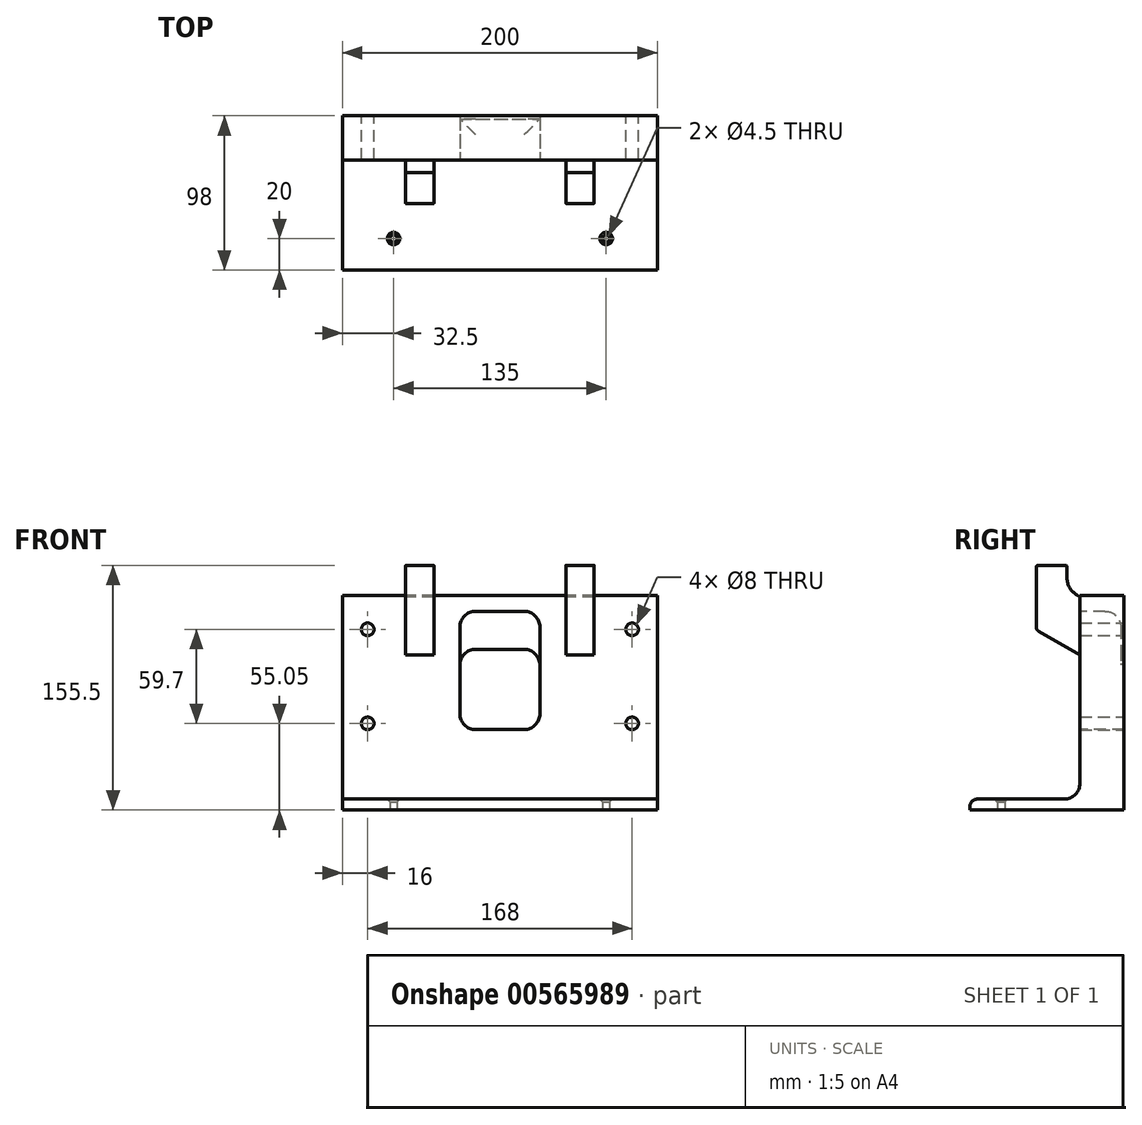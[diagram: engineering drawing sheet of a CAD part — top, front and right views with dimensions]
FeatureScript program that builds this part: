
annotation { "Feature Type Name" : "Feature", "Feature Type Description" : "" }
export const myFeature = defineFeature(function(context is Context, id is Id, definition is map)
    precondition{}
    {
        {
            var Q0;
            Q0=qCreatedBy(makeId("Right.planeOp"),FACE);
            var sketch = newSketch(context, id + "F0", { "sketchPlane" : qUnion([Q0])});
            skLineSegment(sketch, "E0.bottom", {"start": v(-28, 136.25) * mm, "end": v(0, 136.25) * mm});
            skLineSegment(sketch, "E0.top", {"start": v(-28, 0) * mm, "end": v(0, 0) * mm});
            skLineSegment(sketch, "E0.left", {"start": v(-28, 136.25) * mm, "end": v(-28, 17) * mm});
            skLineSegment(sketch, "E0.right", {"start": v(0, 136.25) * mm, "end": v(0, 0) * mm});
            skLineSegment(sketch, "E1.bottom", {"start": v(-28, 0) * mm, "end": v(-98, 0) * mm});
            skLineSegment(sketch, "E1.top", {"start": v(-38, 7) * mm, "end": v(-98, 7) * mm});
            skLineSegment(sketch, "E1.right", {"start": v(-98, 0) * mm, "end": v(-98, 7) * mm});
            skPoint(sketch, "E2.visualSharp", {"position": v(-28, 7) * mm});
            skArc(sketch, "E2.filletArc", {"start": v(-38, 7) * mm, "mid": v(-30.93, 9.93) * mm, "end": v(-28, 17) * mm});
            skSolve(sketch);
        }
        {
            var Q0;
            Q0 = qSketchRegion(id + "F0", true);
            extrude(context, id + "F1", {"entities" : qUnion([Q0]), "endBound" : BoundingType.SYMMETRIC, "depth" : 200 * mm, "offsetDistance" : 25 * mm});
        }
        {
            var Q0;
            Q0=qCreatedBy(makeId("Right.planeOp"),FACE);
            var sketch = newSketch(context, id + "F2", { "sketchPlane" : qUnion([Q0])});
            skLineSegment(sketch, "E3", {"start": v(48.15, 106.49) * mm, "end": v(19.58, 28) * mm});
            skLineSegment(sketch, "E4", {"start": v(19.58, 28) * mm, "end": v(19.58, 0) * mm});
            skLineSegment(sketch, "E5", {"start": v(19.58, 0) * mm, "end": v(0, 0) * mm});
            skLineSegment(sketch, "E6", {"start": v(46.5, 110) * mm, "end": v(0, 126.94) * mm});
            skLineSegment(sketch, "E7", {"start": v(0, 126.94) * mm, "end": v(0, 0) * mm});
            skPoint(sketch, "E8.visualSharp", {"position": v(49.1, 109.07) * mm});
            skArc(sketch, "E8.filletArc", {"start": v(48.15, 106.49) * mm, "mid": v(48.06, 108.59) * mm, "end": v(46.5, 110.01) * mm});
            skLineSegment(sketch, "E9.0", {"start": v(45.25, 107.28) * mm, "end": v(0, 123.74) * mm});
            skLineSegment(sketch, "E9.1", {"start": v(45.25, 107.28) * mm, "end": v(16.58, 28.53) * mm});
            skLineSegment(sketch, "E9.2", {"start": v(16.58, 28.53) * mm, "end": v(16.58, 3) * mm});
            skLineSegment(sketch, "E9.3", {"start": v(16.58, 3) * mm, "end": v(0, 3) * mm});
            skSolve(sketch);
        }
        {
            var Q0;
            Q0=makeQuery(id+"F2.imprint","IMPRINT",FACE,{"disambiguationData":[TD([[makeQuery(id+"F2.imprint","IMPRINT",EDGE,{"derivedFrom":sQuery(id+"F2.wireOp",EDGE,"E3")}),-1.0]])]});
            extrude(context, id + "F3", {"entities" : qUnion([Q0]), "operationType" : NewBodyOperationType.ADD, "endBound" : BoundingType.SYMMETRIC, "depth" : 85 * mm, "offsetDistance" : 25 * mm});
        }
        {
            var Q0;
            Q0=makeQuery(id+"F3.opExtrude","SWEPT_FACE",FACE,{"disambiguationData":[OSD([sQuery(id+"F2.wireOp",EDGE,"E3")])]});
            var sketch = newSketch(context, id + "F4", { "sketchPlane" : qUnion([Q0])});
            skLineSegment(sketch, "E10.bottom", {"start": v(-9.95, 93.91) * mm, "end": v(9.95, 93.91) * mm});
            skLineSegment(sketch, "E10.top", {"start": v(-9.95, 62.51) * mm, "end": v(9.95, 62.51) * mm});
            skLineSegment(sketch, "E10.left", {"start": v(-15.7, 88.16) * mm, "end": v(-15.7, 68.26) * mm});
            skLineSegment(sketch, "E10.right", {"start": v(15.7, 88.16) * mm, "end": v(15.7, 68.26) * mm});
            skLineSegment(sketch, "E11", {"start": v(0, 62.51) * mm, "end": v(0, 0) * mm, "construction": true});
            skCircle(sketch, "E12", {"center": v(19.05, 108.21) * mm, "radius": 2.1 * mm});
            skCircle(sketch, "E13", {"center": v(9.53, 108.21) * mm, "radius": 2.4 * mm});
            skCircle(sketch, "E14", {"center": v(-19.05, 108.21) * mm, "radius": 2.1 * mm});
            skCircle(sketch, "E15", {"center": v(-19.05, 48.21) * mm, "radius": 2.1 * mm});
            skCircle(sketch, "E16", {"center": v(9.53, 48.21) * mm, "radius": 2.4 * mm});
            skCircle(sketch, "E17", {"center": v(19.05, 48.21) * mm, "radius": 2.1 * mm});
            skPoint(sketch, "E18.visualSharp", {"position": v(-15.7, 93.91) * mm});
            skArc(sketch, "E18.filletArc", {"start": v(-9.95, 93.91) * mm, "mid": v(-14.02, 92.23) * mm, "end": v(-15.7, 88.16) * mm});
            skPoint(sketch, "E19.visualSharp", {"position": v(15.7, 93.91) * mm});
            skArc(sketch, "E19.filletArc", {"start": v(15.7, 88.16) * mm, "mid": v(14.02, 92.23) * mm, "end": v(9.95, 93.91) * mm});
            skPoint(sketch, "E20.visualSharp", {"position": v(-15.7, 62.51) * mm});
            skArc(sketch, "E20.filletArc", {"start": v(-15.7, 68.26) * mm, "mid": v(-14.02, 64.2) * mm, "end": v(-9.95, 62.51) * mm});
            skPoint(sketch, "E21.visualSharp", {"position": v(15.7, 62.51) * mm});
            skArc(sketch, "E21.filletArc", {"start": v(9.95, 62.51) * mm, "mid": v(14.02, 64.2) * mm, "end": v(15.7, 68.26) * mm});
            skCircle(sketch, "E22", {"center": v(-33, 78.21) * mm, "radius": 2.75 * mm});
            skPoint(sketch, "E22.centerSnap0", {"position": v(-15.7, 78.21) * mm});
            skCircle(sketch, "E23", {"center": v(33, 78.21) * mm, "radius": 2.75 * mm});
            skPoint(sketch, "E23.centerSnap0", {"position": v(15.7, 78.21) * mm});
            skLineSegment(sketch, "E24", {"start": v(0, 78.21) * mm, "end": v(-33, 78.21) * mm, "construction": true});
            skLineSegment(sketch, "E25", {"start": v(0, 78.21) * mm, "end": v(33, 78.21) * mm, "construction": true});
            skSolve(sketch);
        }
        {
            var Q0;
            Q0 = qSketchRegion(id + "F4", true);
            extrude(context, id + "F5", {"entities" : qUnion([Q0]), "operationType" : NewBodyOperationType.REMOVE, "oppositeDirection" : true, "depth" : 25 * mm, "offsetDistance" : 25 * mm});
        }
        {
            var Q0;
            Q0=makeQuery(id+"F3.opExtrude","CAP_FACE",FACE,{"disambiguationData":[OSD([sQuery(id+"F2.wireOp",EDGE,"E3"),sQuery(id+"F2.wireOp",EDGE,"E4"),sQuery(id+"F2.wireOp",EDGE,"E5"),sQuery(id+"F2.wireOp",EDGE,"E6"),sQuery(id+"F2.wireOp",EDGE,"E7"),sQuery(id+"F2.wireOp",EDGE,"E8.filletArc"),sQuery(id+"F2.wireOp",EDGE,"E9.0"),sQuery(id+"F2.wireOp",EDGE,"E9.1"),sQuery(id+"F2.wireOp",EDGE,"E9.2"),sQuery(id+"F2.wireOp",EDGE,"E9.3")])],"isStart":false});
            var sketch = newSketch(context, id + "F6", { "sketchPlane" : qUnion([Q0])});
            skLineSegment(sketch, "E26", {"start": v(0, 126.94) * mm, "end": v(46.5, 110) * mm});
            skLineSegment(sketch, "E27", {"start": v(48.15, 106.49) * mm, "end": v(19.58, 28) * mm});
            skLineSegment(sketch, "E28", {"start": v(19.58, 28) * mm, "end": v(19.58, 0) * mm});
            skLineSegment(sketch, "E29", {"start": v(19.58, 0) * mm, "end": v(0, 0) * mm});
            skLineSegment(sketch, "E30", {"start": v(0, 0) * mm, "end": v(0, 126.94) * mm});
            skArc(sketch, "E31", {"start": v(48.15, 106.49) * mm, "mid": v(48.06, 108.59) * mm, "end": v(46.5, 110) * mm});
            skSolve(sketch);
        }
        {
            var Q0;
            Q0 = qSketchRegion(id + "F6", true);
            extrude(context, id + "F7", {"entities" : qUnion([Q0]), "operationType" : NewBodyOperationType.ADD, "depth" : 5 * mm, "offsetDistance" : 25 * mm});
        }
        {
            var Q0;
            Q0=makeQuery(id+"F3.opExtrude","CAP_FACE",FACE,{"disambiguationData":[OSD([sQuery(id+"F2.wireOp",EDGE,"E3"),sQuery(id+"F2.wireOp",EDGE,"E4"),sQuery(id+"F2.wireOp",EDGE,"E5"),sQuery(id+"F2.wireOp",EDGE,"E6"),sQuery(id+"F2.wireOp",EDGE,"E7"),sQuery(id+"F2.wireOp",EDGE,"E8.filletArc"),sQuery(id+"F2.wireOp",EDGE,"E9.0"),sQuery(id+"F2.wireOp",EDGE,"E9.1"),sQuery(id+"F2.wireOp",EDGE,"E9.2"),sQuery(id+"F2.wireOp",EDGE,"E9.3")])],"isStart":true});
            var sketch = newSketch(context, id + "F8", { "sketchPlane" : qUnion([Q0])});
            skLineSegment(sketch, "E32", {"start": v(-46.5, 110) * mm, "end": v(0, 126.94) * mm});
            skLineSegment(sketch, "E33", {"start": v(0, 126.94) * mm, "end": v(0, 0) * mm});
            skLineSegment(sketch, "E34", {"start": v(0, 0) * mm, "end": v(-19.58, 0) * mm});
            skLineSegment(sketch, "E35", {"start": v(-19.58, 0) * mm, "end": v(-19.58, 28) * mm});
            skLineSegment(sketch, "E36", {"start": v(-19.58, 28) * mm, "end": v(-48.15, 106.49) * mm});
            skArc(sketch, "E37", {"start": v(-46.5, 110) * mm, "mid": v(-48.06, 108.59) * mm, "end": v(-48.15, 106.49) * mm});
            skSolve(sketch);
        }
        {
            var Q0;
            Q0 = qSketchRegion(id + "F8", true);
            extrude(context, id + "F9", {"entities" : qUnion([Q0]), "operationType" : NewBodyOperationType.ADD, "depth" : 5 * mm, "offsetDistance" : 25 * mm});
        }
        {
            var Q0;
            Q0=makeQuery(id+"F1.opExtrude","SWEPT_FACE",FACE,{"disambiguationData":[OSD([sQuery(id+"F0.wireOp",EDGE,"E0.left")])]});
            var sketch = newSketch(context, id + "F10", { "sketchPlane" : qUnion([Q0])});
            skLineSegment(sketch, "E38.bottom", {"start": v(-15.38, 126.25) * mm, "end": v(15.38, 126.25) * mm});
            skLineSegment(sketch, "E38.top", {"start": v(-15.38, 51.1) * mm, "end": v(15.38, 51.1) * mm});
            skLineSegment(sketch, "E38.left", {"start": v(-25.38, 116.25) * mm, "end": v(-25.38, 61.1) * mm});
            skLineSegment(sketch, "E38.right", {"start": v(25.38, 116.25) * mm, "end": v(25.38, 61.1) * mm});
            skPoint(sketch, "E39.visualSharp", {"position": v(-25.38, 126.25) * mm});
            skArc(sketch, "E39.filletArc", {"start": v(-15.38, 126.25) * mm, "mid": v(-22.45, 123.32) * mm, "end": v(-25.38, 116.25) * mm});
            skPoint(sketch, "E40.visualSharp", {"position": v(25.38, 126.25) * mm});
            skArc(sketch, "E40.filletArc", {"start": v(25.38, 116.25) * mm, "mid": v(22.45, 123.32) * mm, "end": v(15.38, 126.25) * mm});
            skPoint(sketch, "E41.visualSharp", {"position": v(25.38, 51.1) * mm});
            skArc(sketch, "E41.filletArc", {"start": v(15.38, 51.1) * mm, "mid": v(22.45, 54.03) * mm, "end": v(25.38, 61.1) * mm});
            skPoint(sketch, "E42.visualSharp", {"position": v(-25.38, 51.1) * mm});
            skArc(sketch, "E42.filletArc", {"start": v(-25.38, 61.1) * mm, "mid": v(-22.45, 54.03) * mm, "end": v(-15.37, 51.1) * mm});
            skLineSegment(sketch, "E43", {"start": v(0, 0) * mm, "end": v(0, 51.1) * mm, "construction": true});
            skPoint(sketch, "E43.endSnap0", {"position": v(0, 51.1) * mm});
            skSolve(sketch);
        }
        {
            var Q0;
            Q0 = qSketchRegion(id + "F10", true);
            extrude(context, id + "F11", {"entities" : qUnion([Q0]), "operationType" : NewBodyOperationType.REMOVE, "oppositeDirection" : true, "depth" : 26 * mm, "offsetDistance" : 25 * mm});
        }
        {
            var Q0;
            Q0=makeQuery(id+"F11.boolean.opBoolean","COPY",FACE,{"derivedFrom":makeQuery(id+"F11.opExtrude","CAP_FACE",FACE,{"disambiguationData":[OSD([sQuery(id+"F10.wireOp",EDGE,"E38.bottom"),sQuery(id+"F10.wireOp",EDGE,"E38.top"),sQuery(id+"F10.wireOp",EDGE,"E38.left"),sQuery(id+"F10.wireOp",EDGE,"E38.right"),sQuery(id+"F10.wireOp",EDGE,"E39.filletArc"),sQuery(id+"F10.wireOp",EDGE,"E40.filletArc"),sQuery(id+"F10.wireOp",EDGE,"E41.filletArc"),sQuery(id+"F10.wireOp",EDGE,"E42.filletArc")])],"isStart":false})});
            var sketch = newSketch(context, id + "F12", { "sketchPlane" : qUnion([Q0])});
            skLineSegment(sketch, "E44.bottom", {"start": v(-15.38, 102.1) * mm, "end": v(15.38, 102.1) * mm});
            skLineSegment(sketch, "E44.top", {"start": v(-15.38, 51.1) * mm, "end": v(15.38, 51.1) * mm});
            skLineSegment(sketch, "E44.left", {"start": v(-25.38, 92.1) * mm, "end": v(-25.38, 61.1) * mm});
            skLineSegment(sketch, "E44.right", {"start": v(25.38, 92.1) * mm, "end": v(25.38, 61.1) * mm});
            skPoint(sketch, "E45.visualSharp", {"position": v(-25.38, 102.1) * mm});
            skArc(sketch, "E45.filletArc", {"start": v(-15.38, 102.1) * mm, "mid": v(-22.45, 99.17) * mm, "end": v(-25.38, 92.1) * mm});
            skPoint(sketch, "E46.visualSharp", {"position": v(25.38, 102.1) * mm});
            skArc(sketch, "E46.filletArc", {"start": v(25.38, 92.1) * mm, "mid": v(22.45, 99.17) * mm, "end": v(15.38, 102.1) * mm});
            skPoint(sketch, "E47.visualSharp", {"position": v(25.38, 51.1) * mm});
            skArc(sketch, "E47.filletArc", {"start": v(15.38, 51.1) * mm, "mid": v(22.45, 54.03) * mm, "end": v(25.38, 61.1) * mm});
            skPoint(sketch, "E48.visualSharp", {"position": v(-25.38, 51.1) * mm});
            skArc(sketch, "E48.filletArc", {"start": v(-25.38, 61.1) * mm, "mid": v(-22.45, 54.03) * mm, "end": v(-15.38, 51.1) * mm});
            skSolve(sketch);
        }
        {
            var Q0;
            Q0 = qSketchRegion(id + "F12", true);
            extrude(context, id + "F13", {"entities" : qUnion([Q0]), "operationType" : NewBodyOperationType.REMOVE, "oppositeDirection" : true, "depth" : 3 * mm, "offsetDistance" : 25 * mm});
        }
        {
            var Q0;
            Q0=makeQuery(id+"F9.boolean.opBoolean","MERGE",EDGE,{"derivedFrom":[makeQuery(id+"F7.boolean.opBoolean","MERGE",EDGE,{"derivedFrom":[makeQuery(id+"F3.opExtrude","SWEPT_EDGE",EDGE,{"disambiguationData":[OSD([sQuery(id+"F2.wireOp",EDGE,"E6"),sQuery(id+"F2.wireOp",EDGE,"E7")])]}),makeQuery(id+"F7.opExtrude","SWEPT_EDGE",EDGE,{"disambiguationData":[OSD([sQuery(id+"F6.wireOp",EDGE,"E26"),sQuery(id+"F6.wireOp",EDGE,"E30")])]})]}),makeQuery(id+"F9.opExtrude","SWEPT_EDGE",EDGE,{"disambiguationData":[OSD([sQuery(id+"F8.wireOp",EDGE,"E32"),sQuery(id+"F8.wireOp",EDGE,"E33")])]})]});
            var Q1;
            Q1=makeQuery(id+"F9.boolean.opBoolean","MERGE",EDGE,{"derivedFrom":[makeQuery(id+"F7.boolean.opBoolean","MERGE",EDGE,{"derivedFrom":[makeQuery(id+"F3.opExtrude","SWEPT_EDGE",EDGE,{"disambiguationData":[OSD([sQuery(id+"F2.wireOp",EDGE,"E3"),sQuery(id+"F2.wireOp",EDGE,"E4")])]}),makeQuery(id+"F7.opExtrude","SWEPT_EDGE",EDGE,{"disambiguationData":[OSD([sQuery(id+"F6.wireOp",EDGE,"E27"),sQuery(id+"F6.wireOp",EDGE,"E28")])]})]}),makeQuery(id+"F9.opExtrude","SWEPT_EDGE",EDGE,{"disambiguationData":[OSD([sQuery(id+"F8.wireOp",EDGE,"E35"),sQuery(id+"F8.wireOp",EDGE,"E36")])]})]});
            fillet(context, id + "F14", {"entities" : qUnion([Q0, Q1]), "tangentPropagation" : true, "radius" : 11.32 * mm, "defaultsChanged" : false, "vertexSettings" : [], "allowEdgeOverflow" : false});
        }
        {
            var Q0;
            Q0=qCreatedBy(makeId("Right.planeOp"),FACE);
            var sketch = newSketch(context, id + "F15", { "sketchPlane" : qUnion([Q0])});
            skLineSegment(sketch, "E49", {"start": v(-28, 98.4) * mm, "end": v(-54.2, 113.52) * mm});
            skLineSegment(sketch, "E50", {"start": v(-55.7, 116.12) * mm, "end": v(-55.7, 154.5) * mm});
            skLineSegment(sketch, "E51", {"start": v(-54.7, 155.5) * mm, "end": v(-37.2, 155.5) * mm});
            skLineSegment(sketch, "E52", {"start": v(-36.2, 154.5) * mm, "end": v(-36.2, 147.42) * mm});
            skLineSegment(sketch, "E53", {"start": v(-29.95, 136.6) * mm, "end": v(-28, 135.47) * mm});
            skLineSegment(sketch, "E54", {"start": v(-28, 135.47) * mm, "end": v(-28, 98.4) * mm});
            skPoint(sketch, "E55.visualSharp", {"position": v(-55.7, 114.39) * mm});
            skArc(sketch, "E55.filletArc", {"start": v(-55.7, 116.12) * mm, "mid": v(-55.3, 114.62) * mm, "end": v(-54.2, 113.52) * mm});
            skPoint(sketch, "E56.visualSharp", {"position": v(-55.7, 155.5) * mm});
            skArc(sketch, "E56.filletArc", {"start": v(-54.7, 155.5) * mm, "mid": v(-55.4, 155.2) * mm, "end": v(-55.7, 154.5) * mm});
            skPoint(sketch, "E57.visualSharp", {"position": v(-36.2, 155.5) * mm});
            skArc(sketch, "E57.filletArc", {"start": v(-36.2, 154.5) * mm, "mid": v(-36.5, 155.2) * mm, "end": v(-37.2, 155.5) * mm});
            skPoint(sketch, "E58.visualSharp", {"position": v(-36.2, 140.2) * mm});
            skArc(sketch, "E58.filletArc", {"start": v(-36.2, 147.42) * mm, "mid": v(-34.53, 141.17) * mm, "end": v(-29.95, 136.6) * mm});
            skSolve(sketch);
        }
        {
            var Q0;
            Q0 = qSketchRegion(id + "F15", true);
            extrude(context, id + "F16", {"entities" : qUnion([Q0]), "operationType" : NewBodyOperationType.ADD, "endBound" : BoundingType.SYMMETRIC, "depth" : 119.75 * mm, "offsetDistance" : 25 * mm});
        }
        {
            var Q0;
            Q0 = qSketchRegion(id + "F15", true);
            extrude(context, id + "F17", {"entities" : qUnion([Q0]), "operationType" : NewBodyOperationType.REMOVE, "endBound" : BoundingType.SYMMETRIC, "oppositeDirection" : true, "depth" : 83.75 * mm, "offsetDistance" : 25 * mm});
        }
        {
            var Q0;
            {var subQ3=sQuery(id+"F0.wireOp",EDGE,"E0.bottom");var subQ8=sQuery(id+"F0.wireOp",EDGE,"E0.right");Q0=makeQuery(id+"F9.boolean.opBoolean","SPLIT",FACE,{"disambiguationData":[TD([makeQuery(id+"F1.opExtrude","SWEPT_FACE",FACE,{"disambiguationData":[OSD([subQ3])]})])],"derivedFrom":makeQuery(id+"F1.opExtrude","SWEPT_FACE",FACE,{"disambiguationData":[OSD([subQ8])]})});}
            var sketch = newSketch(context, id + "F18", { "sketchPlane" : qUnion([Q0])});
            skLineSegment(sketch, "E59.bottom", {"start": v(-42.5, 106.49) * mm, "end": v(42.5, 106.49) * mm});
            skLineSegment(sketch, "E59.top", {"start": v(-42.5, 136.25) * mm, "end": v(42.5, 136.25) * mm});
            skLineSegment(sketch, "E59.left", {"start": v(-42.5, 106.49) * mm, "end": v(-42.5, 136.25) * mm});
            skLineSegment(sketch, "E59.right", {"start": v(42.5, 106.49) * mm, "end": v(42.5, 136.25) * mm});
            skSolve(sketch);
        }
        {
            var Q0;
            Q0 = qSketchRegion(id + "F18", true);
            extrude(context, id + "F19", {"entities" : qUnion([Q0]), "operationType" : NewBodyOperationType.REMOVE, "depth" : 100.8 * mm, "offsetDistance" : 25 * mm});
        }
        {
            var Q0;
            Q0=makeQuery(id+"F19.boolean.opBoolean","MERGE",EDGE,{"derivedFrom":[makeQuery(id+"F9.opExtrude","CAP_EDGE",EDGE,{"disambiguationData":[OSD([sQuery(id+"F8.wireOp",EDGE,"E33")])],"isStart":true})],"fromTools":[makeQuery(id+"F19.opExtrude","CAP_EDGE",EDGE,{"disambiguationData":[OSD([sQuery(id+"F18.wireOp",EDGE,"E59.right")])],"isStart":true})]});
            var Q1;
            Q1=makeQuery(id+"F3.opExtrude","CAP_EDGE",EDGE,{"disambiguationData":[OSD([sQuery(id+"F2.wireOp",EDGE,"E9.1")])],"isStart":true});
            var Q2;
            Q2=makeQuery(id+"F3.opExtrude","CAP_EDGE",EDGE,{"disambiguationData":[OSD([sQuery(id+"F2.wireOp",EDGE,"E9.2")])],"isStart":true});
            var Q3;
            Q3=makeQuery(id+"F19.boolean.opBoolean","MERGE",EDGE,{"derivedFrom":[makeQuery(id+"F7.opExtrude","CAP_EDGE",EDGE,{"disambiguationData":[OSD([sQuery(id+"F6.wireOp",EDGE,"E30")])],"isStart":true})],"fromTools":[makeQuery(id+"F19.opExtrude","CAP_EDGE",EDGE,{"disambiguationData":[OSD([sQuery(id+"F18.wireOp",EDGE,"E59.left")])],"isStart":true})]});
            var Q4;
            Q4=makeQuery(id+"F3.opExtrude","CAP_EDGE",EDGE,{"disambiguationData":[OSD([sQuery(id+"F2.wireOp",EDGE,"E9.1")])],"isStart":false});
            var Q5;
            Q5=makeQuery(id+"F3.opExtrude","CAP_EDGE",EDGE,{"disambiguationData":[OSD([sQuery(id+"F2.wireOp",EDGE,"E9.2")])],"isStart":false});
            var Q6;
            Q6=makeQuery(id+"F7.opExtrude","CAP_EDGE",EDGE,{"disambiguationData":[OSD([sQuery(id+"F6.wireOp",EDGE,"E30")])],"isStart":false});
            var Q7;
            Q7=makeQuery(id+"F9.opExtrude","CAP_EDGE",EDGE,{"disambiguationData":[OSD([sQuery(id+"F8.wireOp",EDGE,"E33")])],"isStart":false});
            fillet(context, id + "F20", {"entities" : qUnion([Q0, Q1, Q2, Q3, Q4, Q5, Q6, Q7]), "tangentPropagation" : true, "radius" : 5 * mm, "defaultsChanged" : false, "vertexSettings" : [], "allowEdgeOverflow" : false});
        }
        {
            var Q0;
            Q0=makeQuery(id+"F3.opExtrude","SWEPT_EDGE",EDGE,{"disambiguationData":[OSD([sQuery(id+"F2.wireOp",EDGE,"E7"),sQuery(id+"F2.wireOp",EDGE,"E9.3")])]});
            var Q1;
            Q1=makeQuery(id+"F19.boolean.opBoolean","COPY",EDGE,{"derivedFrom":makeQuery(id+"F19.opExtrude","SWEPT_EDGE",EDGE,{"disambiguationData":[OSD([sQuery(id+"F18.wireOp",EDGE,"E59.bottom"),sQuery(id+"F18.wireOp",EDGE,"E59.left")])]})});
            var Q2;
            Q2=makeQuery(id+"F19.boolean.opBoolean","COPY",EDGE,{"derivedFrom":makeQuery(id+"F19.opExtrude","SWEPT_EDGE",EDGE,{"disambiguationData":[OSD([sQuery(id+"F18.wireOp",EDGE,"E59.bottom"),sQuery(id+"F18.wireOp",EDGE,"E59.right")])]})});
            var Q3;
            {var subQ0=sQuery(id+"F15.wireOp",EDGE,"E54");var subQ1=sQuery(id+"F15.wireOp",EDGE,"E49");var subQ2=makeQuery(id+"F16.opExtrude","SWEPT_FACE",FACE,{"disambiguationData":[OSD([subQ1])]});var subQ3=makeQuery(id+"F1.opExtrude","SWEPT_FACE",FACE,{"disambiguationData":[OSD([sQuery(id+"F0.wireOp",EDGE,"E0.left")])]});Q3=makeQuery(id+"F16.boolean.opBoolean","SPLIT",EDGE,{"disambiguationData":[topologyDisambiguationEdgeConnected([subQ3,subQ2]),TD([makeQuery(id+"F11.boolean.opBoolean","COPY",FACE,{"derivedFrom":makeQuery(id+"F11.opExtrude","SWEPT_FACE",FACE,{"disambiguationData":[OSD([sQuery(id+"F10.wireOp",EDGE,"E38.left")])]})})])],"derivedFrom":makeQuery(id+"F16.opExtrude","SWEPT_EDGE",EDGE,{"disambiguationData":[OSD([subQ1,subQ0])]})});}
            var Q4;
            {var subQ0=sQuery(id+"F15.wireOp",EDGE,"E54");var subQ1=sQuery(id+"F15.wireOp",EDGE,"E49");var subQ2=makeQuery(id+"F16.opExtrude","SWEPT_FACE",FACE,{"disambiguationData":[OSD([subQ1])]});var subQ3=makeQuery(id+"F1.opExtrude","SWEPT_FACE",FACE,{"disambiguationData":[OSD([sQuery(id+"F0.wireOp",EDGE,"E0.left")])]});Q4=makeQuery(id+"F16.boolean.opBoolean","SPLIT",EDGE,{"disambiguationData":[topologyDisambiguationEdgeConnected([subQ3,subQ2]),TD([makeQuery(id+"F11.boolean.opBoolean","COPY",FACE,{"derivedFrom":makeQuery(id+"F11.opExtrude","SWEPT_FACE",FACE,{"disambiguationData":[OSD([sQuery(id+"F10.wireOp",EDGE,"E38.right")])]})})])],"derivedFrom":makeQuery(id+"F16.opExtrude","SWEPT_EDGE",EDGE,{"disambiguationData":[OSD([subQ1,subQ0])]})});}
            var Q5;
            Q5=makeQuery(id+"F16.opExtrude","CAP_EDGE",EDGE,{"disambiguationData":[OSD([sQuery(id+"F15.wireOp",EDGE,"E54")])],"isStart":false});
            var Q6;
            Q6=makeQuery(id+"F16.opExtrude","CAP_EDGE",EDGE,{"disambiguationData":[OSD([sQuery(id+"F15.wireOp",EDGE,"E54")])],"isStart":true});
            var Q7;
            Q7=makeQuery(id+"F1.opExtrude","SWEPT_EDGE",EDGE,{"disambiguationData":[OSD([sQuery(id+"F0.wireOp",EDGE,"E1.top"),sQuery(id+"F0.wireOp",EDGE,"E1.right")])]});
            fillet(context, id + "F21", {"entities" : qUnion([Q0, Q1, Q2, Q3, Q4, Q5, Q6, Q7]), "tangentPropagation" : true, "radius" : 5 * mm, "defaultsChanged" : false, "vertexSettings" : [], "allowEdgeOverflow" : false});
        }
        {
            var Q0;
            Q0=makeQuery(id+"F11.boolean.opBoolean","COPY",EDGE,{"derivedFrom":makeQuery(id+"F11.opExtrude","CAP_EDGE",EDGE,{"disambiguationData":[OSD([sQuery(id+"F10.wireOp",EDGE,"E38.bottom")])],"isStart":false})});
            fillet(context, id + "F22", {"entities" : qUnion([Q0]), "radius" : 10 * mm, "defaultsChanged" : true, "vertexSettings" : [], "allowEdgeOverflow" : false});
        }
        {
            var Q0;
            Q0=qCreatedBy(makeId("Top.planeOp"),FACE);
            var sketch = newSketch(context, id + "F23", { "sketchPlane" : qUnion([Q0])});
            skCircle(sketch, "E60", {"center": v(-67.5, -78) * mm, "radius": 2.25 * mm});
            skCircle(sketch, "E61", {"center": v(67.5, -78) * mm, "radius": 2.25 * mm});
            skLineSegment(sketch, "E62", {"start": v(0, 0) * mm, "end": v(-67.5, -78) * mm, "construction": true});
            skLineSegment(sketch, "E63", {"start": v(0, 0) * mm, "end": v(67.5, -78) * mm, "construction": true});
            skLineSegment(sketch, "E64", {"start": v(-67.5, -78) * mm, "end": v(67.5, -78) * mm, "construction": true});
            skLineSegment(sketch, "E65", {"start": v(0, -78) * mm, "end": v(0, 0) * mm, "construction": true});
            skSolve(sketch);
        }
        {
            var Q0;
            Q0 = qSketchRegion(id + "F23", true);
            extrude(context, id + "F24", {"entities" : qUnion([Q0]), "operationType" : NewBodyOperationType.REMOVE, "depth" : 25 * mm, "offsetDistance" : 25 * mm});
        }
        {
            var Q0;
            Q0=makeQuery(id+"F24.boolean.opBoolean","INTERSECT",EDGE,{"derivedFrom":[makeQuery(id+"F1.opExtrude","SWEPT_FACE",FACE,{"disambiguationData":[OSD([sQuery(id+"F0.wireOp",EDGE,"E1.top")])]}),makeQuery(id+"F24.opExtrude","SWEPT_FACE",FACE,{"disambiguationData":[OSD([sQuery(id+"F23.wireOp",EDGE,"E60")])]})]});
            var Q1;
            Q1=makeQuery(id+"F24.boolean.opBoolean","INTERSECT",EDGE,{"derivedFrom":[makeQuery(id+"F1.opExtrude","SWEPT_FACE",FACE,{"disambiguationData":[OSD([sQuery(id+"F0.wireOp",EDGE,"E1.top")])]}),makeQuery(id+"F24.opExtrude","SWEPT_FACE",FACE,{"disambiguationData":[OSD([sQuery(id+"F23.wireOp",EDGE,"E61")])]})]});
            chamfer(context, id + "F25", {"entities" : qUnion([Q0, Q1]), "width" : 1.7 * mm, "tangentPropagation" : true});
        }
        {
            var Q0;
            Q0=qCreatedBy(makeId("Right.planeOp"),FACE);
            var sketch = newSketch(context, id + "F26", { "sketchPlane" : qUnion([Q0])});
            skLineSegment(sketch, "E66.bottom", {"start": v(48.32, 136.25) * mm, "end": v(0, 136.25) * mm});
            skLineSegment(sketch, "E66.top", {"start": v(48.32, 0) * mm, "end": v(0, 0) * mm});
            skLineSegment(sketch, "E66.left", {"start": v(48.32, 136.25) * mm, "end": v(48.32, 0) * mm});
            skLineSegment(sketch, "E66.right", {"start": v(0, 136.25) * mm, "end": v(0, 0) * mm});
            skSolve(sketch);
        }
        {
            var Q0;
            Q0 = qSketchRegion(id + "F26", true);
            extrude(context, id + "F27", {"entities" : qUnion([Q0]), "operationType" : NewBodyOperationType.REMOVE, "endBound" : BoundingType.SYMMETRIC, "oppositeDirection" : true, "depth" : 200 * mm, "offsetDistance" : 25 * mm});
        }
        {
            var Q0;
            {var subQ7=sQuery(id+"F0.wireOp",EDGE,"E0.bottom");var subQ12=sQuery(id+"F0.wireOp",EDGE,"E0.right");var subQ20=makeQuery(id+"F1.opExtrude","SWEPT_FACE",FACE,{"disambiguationData":[OSD([subQ12])]});Q0=makeQuery(id+"F27.boolean.opBoolean","MERGE",FACE,{"derivedFrom":[makeQuery(id+"F19.boolean.opBoolean","MERGE",FACE,{"derivedFrom":[makeQuery(id+"F9.boolean.opBoolean","SPLIT",FACE,{"disambiguationData":[TD([makeQuery(id+"F3.opExtrude","SWEPT_FACE",FACE,{"disambiguationData":[OSD([sQuery(id+"F2.wireOp",EDGE,"E9.0")])]})])],"derivedFrom":subQ20}),makeQuery(id+"F9.boolean.opBoolean","SPLIT",FACE,{"disambiguationData":[TD([makeQuery(id+"F1.opExtrude","SWEPT_FACE",FACE,{"disambiguationData":[OSD([subQ7])]})])],"derivedFrom":subQ20})],"fromTools":[makeQuery(id+"F19.opExtrude","CAP_FACE",FACE,{"disambiguationData":[OSD([sQuery(id+"F18.wireOp",EDGE,"E59.bottom"),sQuery(id+"F18.wireOp",EDGE,"E59.top"),sQuery(id+"F18.wireOp",EDGE,"E59.left"),sQuery(id+"F18.wireOp",EDGE,"E59.right")])],"isStart":true})]})],"fromTools":[makeQuery(id+"F27.opExtrude","SWEPT_FACE",FACE,{"disambiguationData":[OSD([sQuery(id+"F26.wireOp",EDGE,"E66.right")])]})]});}
            var sketch = newSketch(context, id + "F28", { "sketchPlane" : qUnion([Q0])});
            skCircle(sketch, "E67", {"center": v(-84, 114.75) * mm, "radius": 4 * mm});
            skCircle(sketch, "E68", {"center": v(84, 114.75) * mm, "radius": 4 * mm});
            skLineSegment(sketch, "E69", {"start": v(-84, 114.75) * mm, "end": v(84, 114.75) * mm, "construction": true});
            skLineSegment(sketch, "E70", {"start": v(0, 114.75) * mm, "end": v(0, 0) * mm, "construction": true});
            skCircle(sketch, "E71", {"center": v(-84, 55.05) * mm, "radius": 4 * mm});
            skCircle(sketch, "E72", {"center": v(84, 55.05) * mm, "radius": 4 * mm});
            skSolve(sketch);
        }
        {
            var Q0;
            Q0 = qSketchRegion(id + "F28", true);
            extrude(context, id + "F29", {"entities" : qUnion([Q0]), "operationType" : NewBodyOperationType.REMOVE, "endBound" : BoundingType.THROUGH_ALL, "oppositeDirection" : true, "depth" : 25 * mm, "offsetDistance" : 25 * mm});
        }
    });
